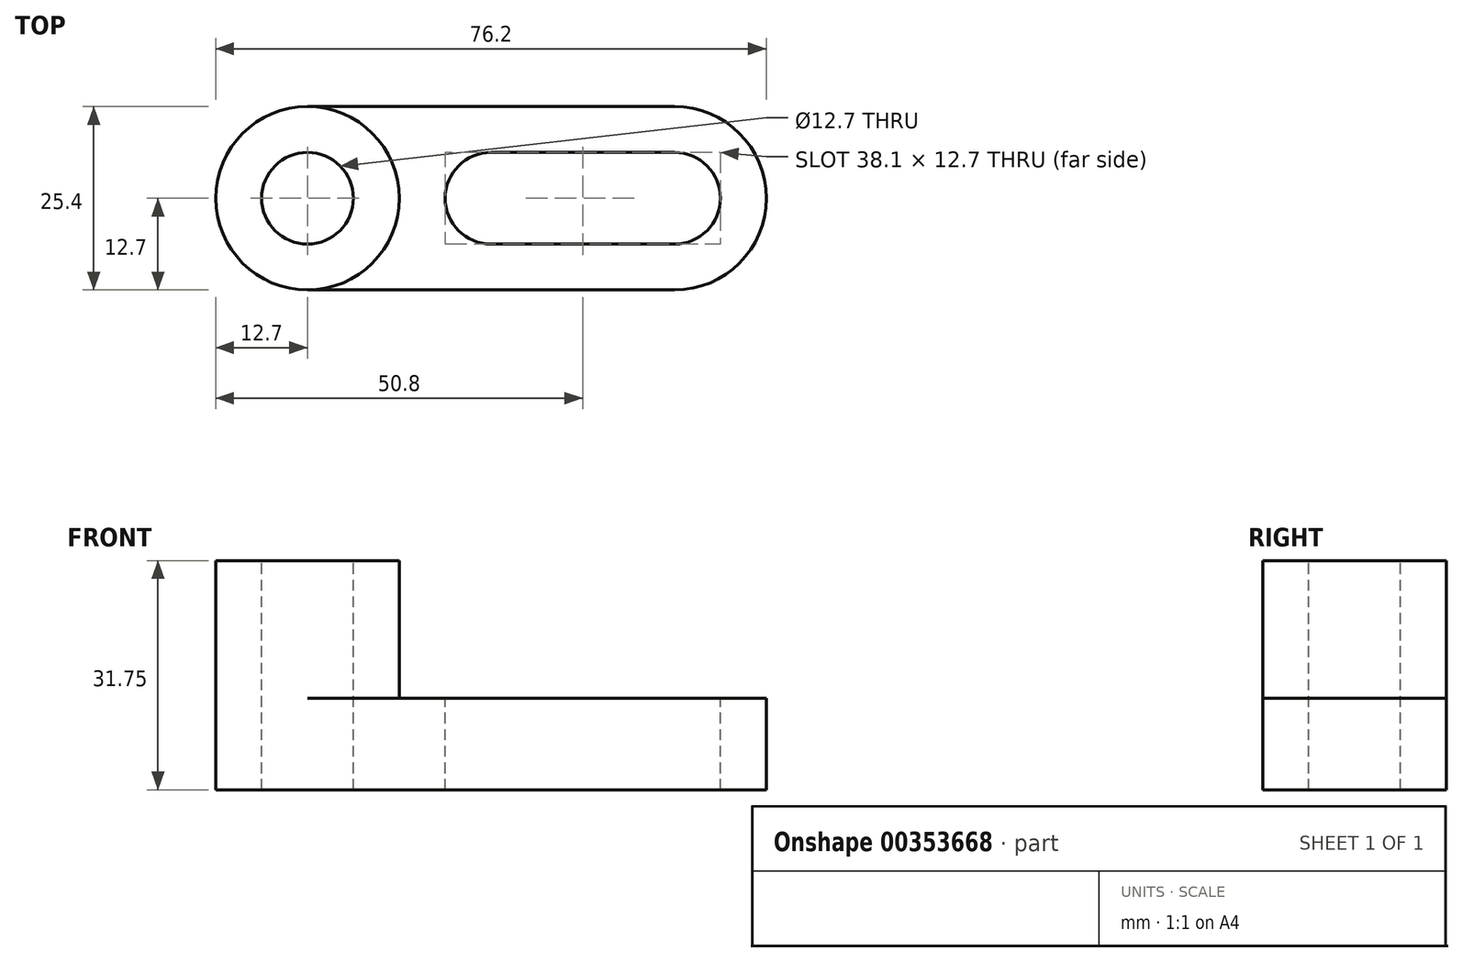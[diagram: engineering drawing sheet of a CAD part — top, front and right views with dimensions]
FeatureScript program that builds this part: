
annotation { "Feature Type Name" : "Feature", "Feature Type Description" : "" }
export const myFeature = defineFeature(function(context is Context, id is Id, definition is map)
    precondition{}
    {
        {
            var Q0;
            Q0=qCreatedBy(makeId("Front.planeOp"),FACE);
            var sketch = newSketch(context, id + "F0", { "sketchPlane" : qUnion([Q0])});
            skLineSegment(sketch, "E0", {"start": v(-75.7, 50.8) * mm, "end": v(-75.7, 0) * mm});
            skLineSegment(sketch, "E1", {"start": v(-75.7, 0) * mm, "end": v(13.2, 0) * mm});
            skLineSegment(sketch, "E2", {"start": v(13.2, 0) * mm, "end": v(13.2, 12.7) * mm});
            skLineSegment(sketch, "E3", {"start": v(13.2, 12.7) * mm, "end": v(-37.6, 12.7) * mm});
            skLineSegment(sketch, "E4", {"start": v(-37.6, 12.7) * mm, "end": v(-37.6, 50.8) * mm});
            skLineSegment(sketch, "E5", {"start": v(-37.6, 50.8) * mm, "end": v(-75.7, 50.8) * mm});
            skSolve(sketch);
        }
        {
            var Q0;
            Q0 = qSketchRegion(id + "F0", true);
            extrude(context, id + "F1", {"entities" : qUnion([Q0]), "depth" : 25.4 * mm});
        }
        {
            var Q0;
            Q0=makeQuery(id+"F1.opExtrude","SWEPT_FACE",FACE,{"disambiguationData":[OSD([sQuery(id+"F0.wireOp",EDGE,"E5")])]});
            var sketch = newSketch(context, id + "F2", { "sketchPlane" : qUnion([Q0])});
            skCircle(sketch, "E6", {"center": v(-56.66, -12.7) * mm, "radius": 6.35 * mm});
            skCircle(sketch, "E7", {"center": v(-56.66, -12.7) * mm, "radius": 12.7 * mm});
            skSolve(sketch);
        }
        {
            var Q0;
            {var subQ1=sQuery(id+"F0.wireOp",EDGE,"E5");var subQ6=makeQuery(id+"F1.opExtrude","SWEPT_EDGE",EDGE,{"disambiguationData":[OSD([sQuery(id+"F0.wireOp",EDGE,"E4"),subQ1])]});Q0=makeQuery(id+"F2.imprint","IMPRINT",FACE,{"disambiguationData":[TD([[makeQuery(id+"F2.imprint","IMPRINT",EDGE,{"derivedFrom":subQ6}),1.0]])]});}
            var Q1;
            Q1=makeQuery(id+"F2.imprint","IMPRINT",FACE,{"disambiguationData":[TD([[makeQuery(id+"F2.imprint","IMPRINT",EDGE,{"derivedFrom":sQuery(id+"F2.wireOp",EDGE,"E6")}),1.0]])]});
            extrude(context, id + "F3", {"entities" : qUnion([Q0, Q1]), "operationType" : NewBodyOperationType.REMOVE, "oppositeDirection" : true, "depth" : 38.1 * mm});
        }
        {
            var Q0;
            Q0=makeQuery(id+"F1.opExtrude","CAP_FACE",FACE,{"disambiguationData":[OSD([sQuery(id+"F0.wireOp",EDGE,"E0"),sQuery(id+"F0.wireOp",EDGE,"E1"),sQuery(id+"F0.wireOp",EDGE,"E2"),sQuery(id+"F0.wireOp",EDGE,"E3"),sQuery(id+"F0.wireOp",EDGE,"E4"),sQuery(id+"F0.wireOp",EDGE,"E5")])],"isStart":false});
            var sketch = newSketch(context, id + "F4", { "sketchPlane" : qUnion([Q0])});
            skArc(sketch, "E8", {"start": v(-75.7, 5.06) * mm, "mid": v(-75.42, 2.37) * mm, "end": v(-74.14, 0) * mm});
            skSolve(sketch);
        }
        {
            var Q0;
            Q0 = qSketchRegion(id + "F4", true);
            var Q1;
            {var subQ0=sQuery(id+"F4.wireOp",EDGE,"E8");var subQ1=makeQuery(id+"F1.opExtrude","CAP_EDGE",EDGE,{"disambiguationData":[OSD([sQuery(id+"F0.wireOp",EDGE,"E1")])],"isStart":false});var subQ2=makeQuery(id+"F4.imprint","INTERSECT",VERTEX,{"derivedFrom":[subQ1,subQ0]});Q1=makeQuery(id+"F4.imprint","IMPRINT",FACE,{"disambiguationData":[TD([[makeQuery(id+"F4.imprint","IMPRINT",EDGE,{"disambiguationData":[TD([[subQ2,1.0]])],"derivedFrom":subQ0}),-1.0]])]});}
            extrude(context, id + "F5", {"entities" : qUnion([Q0, Q1]), "operationType" : NewBodyOperationType.REMOVE, "oppositeDirection" : true, "depth" : 25.4 * mm});
        }
        {
            var Q0;
            Q0=makeQuery(id+"F1.opExtrude","SWEPT_FACE",FACE,{"disambiguationData":[OSD([sQuery(id+"F0.wireOp",EDGE,"E5")])]});
            var sketch = newSketch(context, id + "F6", { "sketchPlane" : qUnion([Q0])});
            skArc(sketch, "E9", {"start": v(-56.66, 0) * mm, "mid": v(-69.36, -12.7) * mm, "end": v(-56.66, -25.4) * mm});
            skSolve(sketch);
        }
        {
            var Q0;
            Q0 = qSketchRegion(id + "F6", true);
            var Q1;
            Q1=makeQuery(id+"F6.imprint","IMPRINT",FACE,{"disambiguationData":[TD([[makeQuery(id+"F6.imprint","IMPRINT",EDGE,{"derivedFrom":sQuery(id+"F6.wireOp",EDGE,"E9")}),-1.0]])]});
            extrude(context, id + "F7", {"entities" : qUnion([Q0, Q1]), "operationType" : NewBodyOperationType.REMOVE, "oppositeDirection" : true, "depth" : 25.4 * mm});
        }
        {
            var Q0;
            Q0=makeQuery(id+"F7.boolean.opBoolean","COPY",FACE,{"derivedFrom":makeQuery(id+"F7.opExtrude","CAP_FACE",FACE,{"disambiguationData":[OSD([sQuery(id+"F0.wireOp",EDGE,"E0"),sQuery(id+"F0.wireOp",EDGE,"E5"),sQuery(id+"F6.wireOp",EDGE,"E9")])],"isStart":false})});
            extrude(context, id + "F8", {"entities" : qUnion([Q0]), "operationType" : NewBodyOperationType.REMOVE, "oppositeDirection" : true, "depth" : 25.4 * mm});
        }
        {
            var Q0;
            Q0=makeQuery(id+"F3.boolean.opBoolean","COPY",FACE,{"derivedFrom":makeQuery(id+"F3.opExtrude","CAP_FACE",FACE,{"disambiguationData":[OSD([sQuery(id+"F2.wireOp",EDGE,"E6")])],"isStart":false})});
            extrude(context, id + "F9", {"entities" : qUnion([Q0]), "operationType" : NewBodyOperationType.REMOVE, "oppositeDirection" : true, "depth" : 25.4 * mm});
        }
        {
            var Q0;
            Q0=makeQuery(id+"F3.boolean.opBoolean","MERGE",FACE,{"derivedFrom":[makeQuery(id+"F1.opExtrude","SWEPT_FACE",FACE,{"disambiguationData":[OSD([sQuery(id+"F0.wireOp",EDGE,"E3")])]}),makeQuery(id+"F3.opExtrude","CAP_FACE",FACE,{"disambiguationData":[OSD([sQuery(id+"F0.wireOp",EDGE,"E4"),sQuery(id+"F0.wireOp",EDGE,"E5"),sQuery(id+"F2.wireOp",EDGE,"E7")])],"isStart":false})]});
            var sketch = newSketch(context, id + "F10", { "sketchPlane" : qUnion([Q0])});
            skCircle(sketch, "E10", {"center": v(-31.26, -12.7) * mm, "radius": 6.35 * mm});
            skCircle(sketch, "E11", {"center": v(-5.86, -12.7) * mm, "radius": 6.35 * mm});
            skArc(sketch, "E12", {"start": v(-5.86, -25.4) * mm, "mid": v(6.84, -12.7) * mm, "end": v(-5.86, 0) * mm});
            skLineSegment(sketch, "E13", {"start": v(-31.26, -6.35) * mm, "end": v(-5.86, -6.35) * mm});
            skLineSegment(sketch, "E14", {"start": v(-31.26, -19.05) * mm, "end": v(-5.86, -19.05) * mm});
            skSolve(sketch);
        }
        {
            var Q0;
            Q0 = qSketchRegion(id + "F10", true);
            var Q1;
            {var subQ0=sQuery(id+"F10.wireOp",EDGE,"E12");Q1=makeQuery(id+"F10.imprint","IMPRINT",FACE,{"disambiguationData":[TD([[makeQuery(id+"F10.imprint","IMPRINT",EDGE,{"derivedFrom":subQ0}),-1.0]])]});}
            extrude(context, id + "F11", {"entities" : qUnion([Q0, Q1]), "operationType" : NewBodyOperationType.REMOVE, "oppositeDirection" : true, "depth" : 25.4 * mm});
        }
        {
            var Q0;
            Q0=makeQuery(id+"F1.opExtrude","SWEPT_FACE",FACE,{"disambiguationData":[OSD([sQuery(id+"F0.wireOp",EDGE,"E5")])]});
            extrude(context, id + "F12", {"entities" : qUnion([Q0]), "operationType" : NewBodyOperationType.REMOVE, "oppositeDirection" : true, "depth" : 19.05 * mm});
        }
    });
